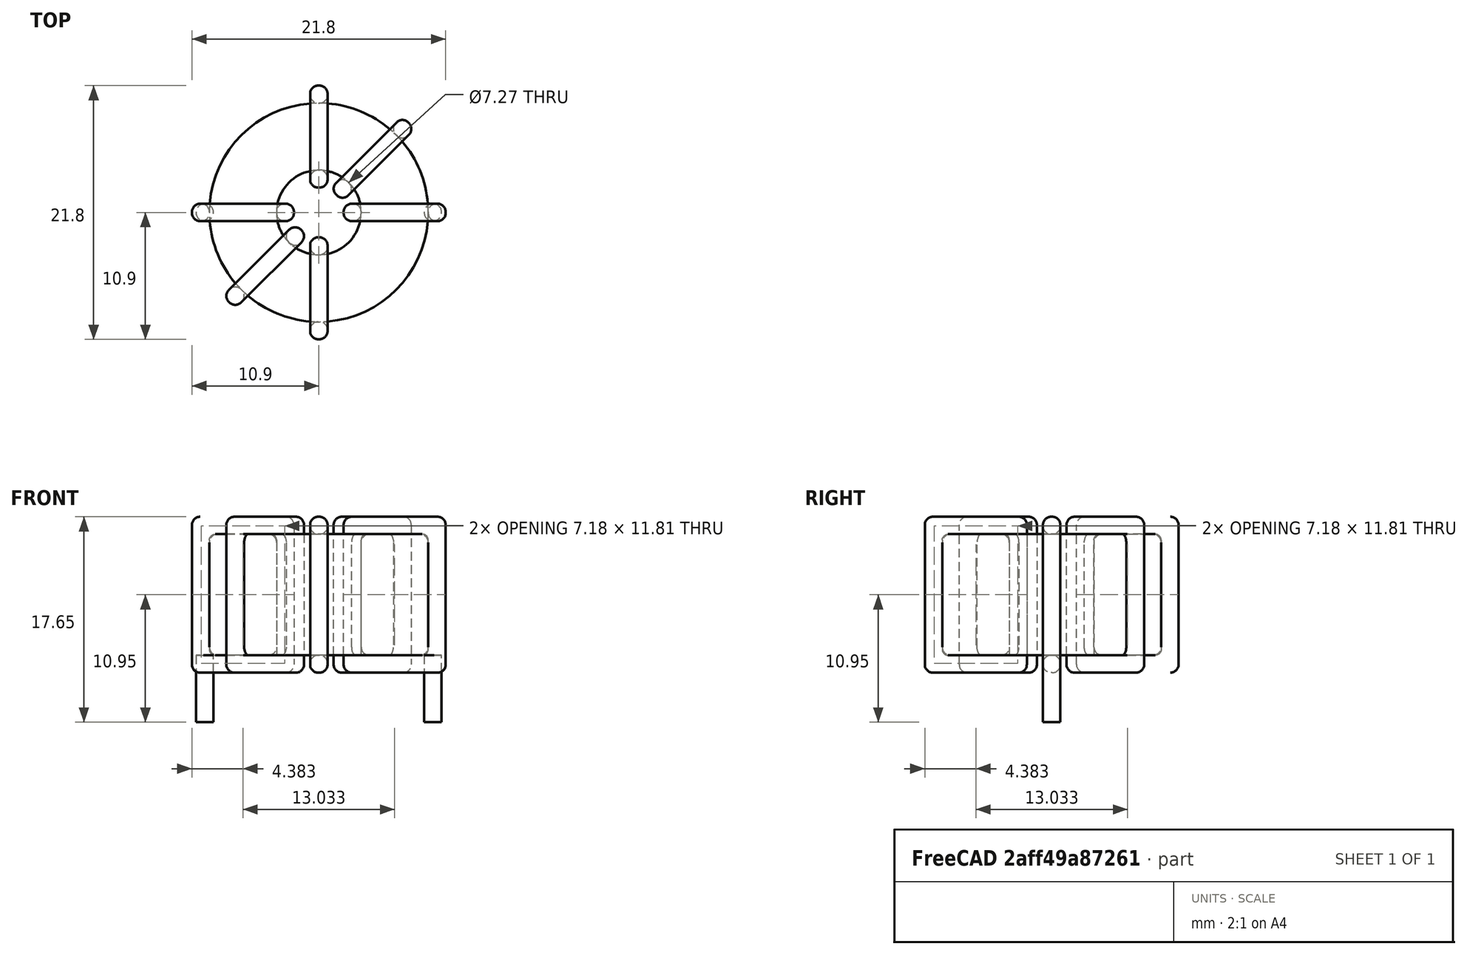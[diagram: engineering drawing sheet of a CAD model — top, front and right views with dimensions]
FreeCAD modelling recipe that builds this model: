
FCSTD DOCUMENT  (FreeCAD 0.16R6703 (Git))
Label: L_Toroid_Horizontal_D21.8mm_P19.60mm_Bourns_2100series
License: All rights reserved
LicenseURL: http://en.wikipedia.org/wiki/All_rights_reserved
objects: Sketcher::SketchObject×6, PartDesign::Pad×6, PartDesign::Fillet×5, Spreadsheet::Sheet×1
note: 23 computed .brp shape members not serialized (recipe doc carries the construction recipe); baked Part::Feature solids carry a one-line shape summary decoded from their .brp

FEATURE [Spreadsheet::Sheet] Spreadsheet  label="dimensions"
  cells = A1=Wx; B1(Wx)=21.8; C1(WW)=7.266666666666667; D1=21.8; A2=Wy; B2(Wy)=21.8; D2=21.8; A3=RM; B3(RMx)=19.6; C3(RMy)=0; A4=d_wire; B4(d_wire)=1.5; A5=H; B5(H)=10.4; A6=offsetx; B6(offsetx)=1.1
FEATURE [Sketcher::SketchObject] Sketch
  Placement = pos=(0,0,2) rot=(0,0,1;0rad)
  expr: Placement.Base.z = 0.5 + Spreadsheet.d_wire
  expr: Constraints[0] = Spreadsheet.Wx / 2 - Spreadsheet.d_wire
  expr: Constraints[4] = Spreadsheet.WW / 2
  expr: Constraints[2] = Spreadsheet.RMy / 2
  expr: Constraints[1] = Spreadsheet.RMx / 2
  sketch-geometry (2):
    g0: Circle CenterX=9.8 CenterY=0 CenterZ=0 NormalX=0 NormalY=0 NormalZ=1 Radius=9.4
    g1: Circle CenterX=9.8 CenterY=0 CenterZ=0 NormalX=0 NormalY=0 NormalZ=1 Radius=3.63333
  constraints (5):
    c: Radius(g0) = 9.4
    c: DistanceX(g-1,g0) = 9.8
    c: DistanceY(g-1,g0) = 0
    c: Coincident(g1,g0)
    c: Radius(g1) = 3.63333
FEATURE [PartDesign::Pad] Pad
  Length = 10.4
  Length2 = 100
  Placement = pos=(0,0,2) rot=(0,0,1;0rad)
  Sketch = -> Sketch
  Type = 0
  expr: Length = Spreadsheet.H
FEATURE [Sketcher::SketchObject] Sketch001
  Placement = pos=(0,0,1.25) rot=(0,0,1;0rad)
  expr: Placement.Base.z = 0.5 + Spreadsheet.d_wire * 0.5
  expr: Constraints[4] = Spreadsheet.RMx
  expr: Constraints[2] = Spreadsheet.RMy
  expr: Constraints[1] = Spreadsheet.d_wire / 2
  sketch-geometry (2):
    g0: Circle CenterX=0 CenterY=0 CenterZ=0 NormalX=0 NormalY=0 NormalZ=1 Radius=0.75
    g1: Circle CenterX=19.6 CenterY=0 CenterZ=0 NormalX=0 NormalY=0 NormalZ=1 Radius=0.75
  constraints (5):
    c: Equal(g0,g1)
    c: Radius(g0) = 0.75
    c: DistanceY(g-1,g1) = 0
    c: Coincident(g0,g-1)
    c: DistanceX(g-1,g1) = 19.6
FEATURE [PartDesign::Pad] Pad001
  Length = 0.75
  Length2 = 5
  Placement = pos=(0,0,1.25) rot=(0,0,1;0rad)
  Reversed = true
  Sketch = -> Sketch001
  Type = 4
  expr: Length2 = 3.5 + Spreadsheet.d_wire
  expr: Length = Spreadsheet.d_wire / 2
FEATURE [PartDesign::Fillet] Fillet
  Base = -> Pad [Edge6,Edge3,Edge2]
  Placement = pos=(0,0,2) rot=(0,0,1;0rad)
  Radius = 0.5
FEATURE [Sketcher::SketchObject] Sketch003
  Placement = pos=(9.8,0,0) rot=(1,0,0;1.5708rad)
  expr: Placement.Base.x = Spreadsheet.RMx / 2
  expr: Constraints[49] = Spreadsheet.Wx - Spreadsheet.d_wire * 2
  expr: Constraints[44] = Spreadsheet.d_wire
  expr: Constraints[23] = Spreadsheet.H
  expr: Constraints[22] = Spreadsheet.Wx / 2 - Spreadsheet.d_wire
  expr: Placement.Base.y = Spreadsheet.RMy / 2
  expr: Constraints[21] = (Spreadsheet.Wx - Spreadsheet.WW) / 2 - Spreadsheet.d_wire
  expr: Constraints[19] = Spreadsheet.d_wire
  expr: Constraints[17] = Spreadsheet.d_wire
  expr: Constraints[18] = Spreadsheet.d_wire
  expr: Constraints[16] = Spreadsheet.d_wire
  sketch-geometry (16):
    g0: LineSegment StartX=-2.13333 StartY=0.5 StartZ=0 EndX=-10.9 EndY=0.5 EndZ=0
    g1: LineSegment StartX=-10.9 StartY=0.5 StartZ=0 EndX=-10.9 EndY=13.9 EndZ=0
    g2: LineSegment StartX=-10.9 StartY=13.9 StartZ=0 EndX=-2.13333 EndY=13.9 EndZ=0
    g3: LineSegment StartX=-2.13333 StartY=13.9 StartZ=0 EndX=-2.13333 EndY=0.5 EndZ=0
    g4: LineSegment StartX=-9.4 StartY=12.4 StartZ=0 EndX=-3.63333 EndY=12.4 EndZ=0
    g5: LineSegment StartX=-3.63333 StartY=12.4 StartZ=0 EndX=-3.63333 EndY=2 EndZ=0
    g6: LineSegment StartX=-3.63333 StartY=2 StartZ=0 EndX=-9.4 EndY=2 EndZ=0
    g7: LineSegment StartX=-9.4 StartY=2 StartZ=0 EndX=-9.4 EndY=12.4 EndZ=0
    g8: LineSegment StartX=2.13333 StartY=13.9 StartZ=0 EndX=10.9 EndY=13.9 EndZ=0
    g9: LineSegment StartX=10.9 StartY=13.9 StartZ=0 EndX=10.9 EndY=0.5 EndZ=0
    g10: LineSegment StartX=10.9 StartY=0.5 StartZ=0 EndX=2.13333 EndY=0.5 EndZ=0
    g11: LineSegment StartX=2.13333 StartY=0.5 StartZ=0 EndX=2.13333 EndY=13.9 EndZ=0
    g12: LineSegment StartX=3.63333 StartY=12.4 StartZ=0 EndX=9.4 EndY=12.4 EndZ=0
    g13: LineSegment StartX=9.4 StartY=12.4 StartZ=0 EndX=9.4 EndY=2 EndZ=0
    g14: LineSegment StartX=9.4 StartY=2 StartZ=0 EndX=3.63333 EndY=2 EndZ=0
    g15: LineSegment StartX=3.63333 StartY=2 StartZ=0 EndX=3.63333 EndY=12.4 EndZ=0
  constraints (50):
    c: Horizontal(g0)
    c: Coincident(g1,g0)
    c: Vertical(g1)
    c: Coincident(g2,g1)
    c: Horizontal(g2)
    c: Coincident(g3,g2)
    c: Coincident(g3,g0)
    c: Vertical(g3)
    c: Coincident(g4,g5)
    c: Coincident(g5,g6)
    c: Coincident(g6,g7)
    c: Coincident(g7,g4)
    c: Horizontal(g4)
    c: Horizontal(g6)
    c: Vertical(g5)
    c: Vertical(g7)
    c: DistanceX(g1,g4) = 1.5
    c: DistanceY(g4,g1) = 1.5
    c: DistanceX(g5,g0) = 1.5
    c: DistanceY(g0,g5) = 1.5
    c: DistanceY(g-1,g0) = 0.5
    c: DistanceX(g6,g6) = 5.76667
    c: DistanceX(g6,g-1) = 9.4
    c: DistanceY(g7,g7) = 10.4
    c: Coincident(g8,g9)
    c: Coincident(g9,g10)
    c: Coincident(g10,g11)
    c: Coincident(g11,g8)
    c: Horizontal(g8)
    c: Horizontal(g10)
    c: Vertical(g9)
    c: Vertical(g11)
    c: Coincident(g12,g13)
    c: Coincident(g13,g14)
    c: Coincident(g14,g15)
    c: Coincident(g15,g12)
    c: Horizontal(g12)
    c: Horizontal(g14)
    c: Vertical(g13)
    c: Vertical(g15)
    c: DistanceY(g8,g2) = 0
    c: DistanceY(g10,g0) = 0
    c: DistanceY(g14,g5) = 0
    c: DistanceY(g12,g4) = 0
    c: DistanceX(g8,g12) = 1.5
    c: Equal(g8,g2)
    c: Equal(g12,g4)
    c: Equal(g9,g1)
    c: Equal(g13,g7)
    c: DistanceX(g4,g12) = 18.8
FEATURE [PartDesign::Pad] Pad002
  Length = 1.5
  Length2 = 100
  Midplane = true
  Placement = pos=(9.8,0,0) rot=(1,0,0;1.5708rad)
  Sketch = -> Sketch003
  Type = 0
  expr: Length = Spreadsheet.d_wire
FEATURE [PartDesign::Fillet] Fillet001
  Base = -> Pad002 [Edge38,Edge41,Edge42,Edge43,Edge29,Edge32,Edge33,Edge34,Edge25,Edge35,Edge36,Edge13,Edge14,Edge15,Edge16,Edge17,Edge18,Edge19,Edge1,Edge2,Edge3,Edge4,Edge5,Edge6,Edge7,Edge37,Edge39,Edge40,Edge20,Edge23,Edge24,Edge21,Edge22,Edge8,Edge9,Edge10,Edge11,Edge12,Edge26,Edge27,+8 more]
  Placement = pos=(9.8,0,0) rot=(1,0,0;1.5708rad)
  Radius = 0.705
  expr: Radius = Spreadsheet.d_wire * 0.47
FEATURE [Sketcher::SketchObject] Sketch004
  Placement = pos=(9.8,0,0) rot=(0.862856,0.357407,0.357407;1.71777rad)
  expr: Placement.Base.x = Spreadsheet.RMx / 2
  expr: Constraints[49] = Spreadsheet.Wx - 2 * Spreadsheet.d_wire
  expr: Constraints[44] = Spreadsheet.d_wire
  expr: Constraints[23] = Spreadsheet.H
  expr: Constraints[22] = Spreadsheet.Wx / 2 - Spreadsheet.d_wire
  expr: Placement.Base.y = Spreadsheet.RMy / 2
  expr: Constraints[21] = (Spreadsheet.Wx - Spreadsheet.WW) / 2 - Spreadsheet.d_wire
  expr: Constraints[19] = Spreadsheet.d_wire
  expr: Constraints[17] = Spreadsheet.d_wire
  expr: Constraints[18] = Spreadsheet.d_wire
  expr: Constraints[16] = Spreadsheet.d_wire
  sketch-geometry (16):
    g0: LineSegment StartX=-2.13333 StartY=0.5 StartZ=0 EndX=-10.9 EndY=0.5 EndZ=0
    g1: LineSegment StartX=-10.9 StartY=0.5 StartZ=0 EndX=-10.9 EndY=13.9 EndZ=0
    g2: LineSegment StartX=-10.9 StartY=13.9 StartZ=0 EndX=-2.13333 EndY=13.9 EndZ=0
    g3: LineSegment StartX=-2.13333 StartY=13.9 StartZ=0 EndX=-2.13333 EndY=0.5 EndZ=0
    g4: LineSegment StartX=-9.4 StartY=12.4 StartZ=0 EndX=-3.63333 EndY=12.4 EndZ=0
    g5: LineSegment StartX=-3.63333 StartY=12.4 StartZ=0 EndX=-3.63333 EndY=2 EndZ=0
    g6: LineSegment StartX=-3.63333 StartY=2 StartZ=0 EndX=-9.4 EndY=2 EndZ=0
    g7: LineSegment StartX=-9.4 StartY=2 StartZ=0 EndX=-9.4 EndY=12.4 EndZ=0
    g8: LineSegment StartX=2.13333 StartY=13.9 StartZ=0 EndX=10.9 EndY=13.9 EndZ=0
    g9: LineSegment StartX=10.9 StartY=13.9 StartZ=0 EndX=10.9 EndY=0.5 EndZ=0
    g10: LineSegment StartX=10.9 StartY=0.5 StartZ=0 EndX=2.13333 EndY=0.5 EndZ=0
    g11: LineSegment StartX=2.13333 StartY=0.5 StartZ=0 EndX=2.13333 EndY=13.9 EndZ=0
    g12: LineSegment StartX=3.63333 StartY=12.4 StartZ=0 EndX=9.4 EndY=12.4 EndZ=0
    g13: LineSegment StartX=9.4 StartY=12.4 StartZ=0 EndX=9.4 EndY=2 EndZ=0
    g14: LineSegment StartX=9.4 StartY=2 StartZ=0 EndX=3.63333 EndY=2 EndZ=0
    g15: LineSegment StartX=3.63333 StartY=2 StartZ=0 EndX=3.63333 EndY=12.4 EndZ=0
  constraints (50):
    c: Horizontal(g0)
    c: Coincident(g1,g0)
    c: Vertical(g1)
    c: Coincident(g2,g1)
    c: Horizontal(g2)
    c: Coincident(g3,g2)
    c: Coincident(g3,g0)
    c: Vertical(g3)
    c: Coincident(g4,g5)
    c: Coincident(g5,g6)
    c: Coincident(g6,g7)
    c: Coincident(g7,g4)
    c: Horizontal(g4)
    c: Horizontal(g6)
    c: Vertical(g5)
    c: Vertical(g7)
    c: DistanceX(g1,g4) = 1.5
    c: DistanceY(g4,g1) = 1.5
    c: DistanceX(g5,g0) = 1.5
    c: DistanceY(g0,g5) = 1.5
    c: DistanceY(g-1,g0) = 0.5
    c: DistanceX(g6,g6) = 5.76667
    c: DistanceX(g6,g-1) = 9.4
    c: DistanceY(g7,g7) = 10.4
    c: Coincident(g8,g9)
    c: Coincident(g9,g10)
    c: Coincident(g10,g11)
    c: Coincident(g11,g8)
    c: Horizontal(g8)
    c: Horizontal(g10)
    c: Vertical(g9)
    c: Vertical(g11)
    c: Coincident(g12,g13)
    c: Coincident(g13,g14)
    c: Coincident(g14,g15)
    c: Coincident(g15,g12)
    c: Horizontal(g12)
    c: Horizontal(g14)
    c: Vertical(g13)
    c: Vertical(g15)
    c: DistanceY(g8,g2) = 0
    c: DistanceY(g10,g0) = 0
    c: DistanceY(g14,g5) = 0
    c: DistanceY(g12,g4) = 0
    c: DistanceX(g8,g12) = 1.5
    c: Equal(g8,g2)
    c: Equal(g12,g4)
    c: Equal(g9,g1)
    c: Equal(g13,g7)
    c: DistanceX(g4,g12) = 18.8
FEATURE [PartDesign::Pad] Pad003
  Length = 1.5
  Length2 = 100
  Midplane = true
  Placement = pos=(9.8,0,0) rot=(0.862856,0.357407,0.357407;1.71777rad)
  Sketch = -> Sketch004
  Type = 0
  expr: Length = Spreadsheet.d_wire
FEATURE [PartDesign::Fillet] Fillet002
  Base = -> Pad003 [Edge38,Edge41,Edge42,Edge43,Edge29,Edge32,Edge33,Edge34,Edge25,Edge35,Edge36,Edge13,Edge14,Edge15,Edge16,Edge17,Edge18,Edge19,Edge1,Edge2,Edge3,Edge4,Edge5,Edge6,Edge7,Edge37,Edge39,Edge40,Edge20,Edge23,Edge24,Edge21,Edge22,Edge8,Edge9,Edge10,Edge11,Edge12,Edge26,Edge27,+8 more]
  Placement = pos=(9.8,0,0) rot=(0.862856,0.357407,0.357407;1.71777rad)
  Radius = 0.705
  expr: Radius = Spreadsheet.d_wire * 0.47
FEATURE [Sketcher::SketchObject] Sketch005
  Placement = pos=(9.8,0,0) rot=(0.862856,-0.357407,-0.357407;1.71777rad)
  expr: Placement.Base.x = Spreadsheet.RMx / 2
  expr: Constraints[49] = Spreadsheet.Wx - 2 * Spreadsheet.d_wire
  expr: Constraints[44] = Spreadsheet.d_wire
  expr: Constraints[23] = Spreadsheet.H
  expr: Constraints[22] = Spreadsheet.Wx / 2 - Spreadsheet.d_wire
  expr: Placement.Base.y = Spreadsheet.RMy / 2
  expr: Constraints[21] = (Spreadsheet.Wx - Spreadsheet.WW) / 2 - Spreadsheet.d_wire
  expr: Constraints[19] = Spreadsheet.d_wire
  expr: Constraints[17] = Spreadsheet.d_wire
  expr: Constraints[18] = Spreadsheet.d_wire
  expr: Constraints[16] = Spreadsheet.d_wire
  sketch-geometry (16):
    g0: LineSegment StartX=-2.13333 StartY=0.5 StartZ=0 EndX=-10.9 EndY=0.5 EndZ=0
    g1: LineSegment StartX=-10.9 StartY=0.5 StartZ=0 EndX=-10.9 EndY=13.9 EndZ=0
    g2: LineSegment StartX=-10.9 StartY=13.9 StartZ=0 EndX=-2.13333 EndY=13.9 EndZ=0
    g3: LineSegment StartX=-2.13333 StartY=13.9 StartZ=0 EndX=-2.13333 EndY=0.5 EndZ=0
    g4: LineSegment StartX=-9.4 StartY=12.4 StartZ=0 EndX=-3.63333 EndY=12.4 EndZ=0
    g5: LineSegment StartX=-3.63333 StartY=12.4 StartZ=0 EndX=-3.63333 EndY=2 EndZ=0
    g6: LineSegment StartX=-3.63333 StartY=2 StartZ=0 EndX=-9.4 EndY=2 EndZ=0
    g7: LineSegment StartX=-9.4 StartY=2 StartZ=0 EndX=-9.4 EndY=12.4 EndZ=0
    g8: LineSegment StartX=2.13333 StartY=13.9 StartZ=0 EndX=10.9 EndY=13.9 EndZ=0
    g9: LineSegment StartX=10.9 StartY=13.9 StartZ=0 EndX=10.9 EndY=0.5 EndZ=0
    g10: LineSegment StartX=10.9 StartY=0.5 StartZ=0 EndX=2.13333 EndY=0.5 EndZ=0
    g11: LineSegment StartX=2.13333 StartY=0.5 StartZ=0 EndX=2.13333 EndY=13.9 EndZ=0
    g12: LineSegment StartX=3.63333 StartY=12.4 StartZ=0 EndX=9.4 EndY=12.4 EndZ=0
    g13: LineSegment StartX=9.4 StartY=12.4 StartZ=0 EndX=9.4 EndY=2 EndZ=0
    g14: LineSegment StartX=9.4 StartY=2 StartZ=0 EndX=3.63333 EndY=2 EndZ=0
    g15: LineSegment StartX=3.63333 StartY=2 StartZ=0 EndX=3.63333 EndY=12.4 EndZ=0
  constraints (50):
    c: Horizontal(g0)
    c: Coincident(g1,g0)
    c: Vertical(g1)
    c: Coincident(g2,g1)
    c: Horizontal(g2)
    c: Coincident(g3,g2)
    c: Coincident(g3,g0)
    c: Vertical(g3)
    c: Coincident(g4,g5)
    c: Coincident(g5,g6)
    c: Coincident(g6,g7)
    c: Coincident(g7,g4)
    c: Horizontal(g4)
    c: Horizontal(g6)
    c: Vertical(g5)
    c: Vertical(g7)
    c: DistanceX(g1,g4) = 1.5
    c: DistanceY(g4,g1) = 1.5
    c: DistanceX(g5,g0) = 1.5
    c: DistanceY(g0,g5) = 1.5
    c: DistanceY(g-1,g0) = 0.5
    c: DistanceX(g6,g6) = 5.76667
    c: DistanceX(g6,g-1) = 9.4
    c: DistanceY(g7,g7) = 10.4
    c: Coincident(g8,g9)
    c: Coincident(g9,g10)
    c: Coincident(g10,g11)
    c: Coincident(g11,g8)
    c: Horizontal(g8)
    c: Horizontal(g10)
    c: Vertical(g9)
    c: Vertical(g11)
    c: Coincident(g12,g13)
    c: Coincident(g13,g14)
    c: Coincident(g14,g15)
    c: Coincident(g15,g12)
    c: Horizontal(g12)
    c: Horizontal(g14)
    c: Vertical(g13)
    c: Vertical(g15)
    c: DistanceY(g8,g2) = 0
    c: DistanceY(g10,g0) = 0
    c: DistanceY(g14,g5) = 0
    c: DistanceY(g12,g4) = 0
    c: DistanceX(g8,g12) = 1.5
    c: Equal(g8,g2)
    c: Equal(g12,g4)
    c: Equal(g9,g1)
    c: Equal(g13,g7)
    c: DistanceX(g4,g12) = 18.8
FEATURE [PartDesign::Pad] Pad004
  Length = 1.5
  Length2 = 100
  Midplane = true
  Placement = pos=(9.8,0,0) rot=(0.862856,-0.357407,-0.357407;1.71777rad)
  Sketch = -> Sketch005
  Type = 0
  expr: Length = Spreadsheet.d_wire
FEATURE [PartDesign::Fillet] Fillet003
  Base = -> Pad004 [Edge38,Edge41,Edge42,Edge43,Edge29,Edge32,Edge33,Edge34,Edge25,Edge35,Edge36,Edge13,Edge14,Edge15,Edge16,Edge17,Edge18,Edge19,Edge1,Edge2,Edge3,Edge4,Edge5,Edge6,Edge7,Edge37,Edge39,Edge40,Edge20,Edge23,Edge24,Edge21,Edge22,Edge8,Edge9,Edge10,Edge11,Edge12,Edge26,Edge27,+8 more]
  Placement = pos=(9.8,0,0) rot=(0.862856,-0.357407,-0.357407;1.71777rad)
  Radius = 0.705
  expr: Radius = Spreadsheet.d_wire * 0.47
FEATURE [Sketcher::SketchObject] Sketch006
  Placement = pos=(9.8,0,0) rot=(0.57735,0.57735,0.57735;2.0944rad)
  expr: Placement.Base.x = Spreadsheet.RMx / 2
  expr: Constraints[49] = Spreadsheet.Wx - Spreadsheet.d_wire * 2
  expr: Constraints[44] = Spreadsheet.d_wire
  expr: Constraints[23] = Spreadsheet.H
  expr: Constraints[22] = Spreadsheet.Wx / 2 - Spreadsheet.d_wire
  expr: Placement.Base.y = Spreadsheet.RMy / 2
  expr: Constraints[21] = (Spreadsheet.Wx - Spreadsheet.WW) / 2 - Spreadsheet.d_wire
  expr: Constraints[19] = Spreadsheet.d_wire
  expr: Constraints[17] = Spreadsheet.d_wire
  expr: Constraints[18] = Spreadsheet.d_wire
  expr: Constraints[16] = Spreadsheet.d_wire
  sketch-geometry (16):
    g0: LineSegment StartX=-2.13333 StartY=0.5 StartZ=0 EndX=-10.9 EndY=0.5 EndZ=0
    g1: LineSegment StartX=-10.9 StartY=0.5 StartZ=0 EndX=-10.9 EndY=13.9 EndZ=0
    g2: LineSegment StartX=-10.9 StartY=13.9 StartZ=0 EndX=-2.13333 EndY=13.9 EndZ=0
    g3: LineSegment StartX=-2.13333 StartY=13.9 StartZ=0 EndX=-2.13333 EndY=0.5 EndZ=0
    g4: LineSegment StartX=-9.4 StartY=12.4 StartZ=0 EndX=-3.63333 EndY=12.4 EndZ=0
    g5: LineSegment StartX=-3.63333 StartY=12.4 StartZ=0 EndX=-3.63333 EndY=2 EndZ=0
    g6: LineSegment StartX=-3.63333 StartY=2 StartZ=0 EndX=-9.4 EndY=2 EndZ=0
    g7: LineSegment StartX=-9.4 StartY=2 StartZ=0 EndX=-9.4 EndY=12.4 EndZ=0
    g8: LineSegment StartX=2.13333 StartY=13.9 StartZ=0 EndX=10.9 EndY=13.9 EndZ=0
    g9: LineSegment StartX=10.9 StartY=13.9 StartZ=0 EndX=10.9 EndY=0.5 EndZ=0
    g10: LineSegment StartX=10.9 StartY=0.5 StartZ=0 EndX=2.13333 EndY=0.5 EndZ=0
    g11: LineSegment StartX=2.13333 StartY=0.5 StartZ=0 EndX=2.13333 EndY=13.9 EndZ=0
    g12: LineSegment StartX=3.63333 StartY=12.4 StartZ=0 EndX=9.4 EndY=12.4 EndZ=0
    g13: LineSegment StartX=9.4 StartY=12.4 StartZ=0 EndX=9.4 EndY=2 EndZ=0
    g14: LineSegment StartX=9.4 StartY=2 StartZ=0 EndX=3.63333 EndY=2 EndZ=0
    g15: LineSegment StartX=3.63333 StartY=2 StartZ=0 EndX=3.63333 EndY=12.4 EndZ=0
  constraints (50):
    c: Horizontal(g0)
    c: Coincident(g1,g0)
    c: Vertical(g1)
    c: Coincident(g2,g1)
    c: Horizontal(g2)
    c: Coincident(g3,g2)
    c: Coincident(g3,g0)
    c: Vertical(g3)
    c: Coincident(g4,g5)
    c: Coincident(g5,g6)
    c: Coincident(g6,g7)
    c: Coincident(g7,g4)
    c: Horizontal(g4)
    c: Horizontal(g6)
    c: Vertical(g5)
    c: Vertical(g7)
    c: DistanceX(g1,g4) = 1.5
    c: DistanceY(g4,g1) = 1.5
    c: DistanceX(g5,g0) = 1.5
    c: DistanceY(g0,g5) = 1.5
    c: DistanceY(g-1,g0) = 0.5
    c: DistanceX(g6,g6) = 5.76667
    c: DistanceX(g6,g-1) = 9.4
    c: DistanceY(g7,g7) = 10.4
    c: Coincident(g8,g9)
    c: Coincident(g9,g10)
    c: Coincident(g10,g11)
    c: Coincident(g11,g8)
    c: Horizontal(g8)
    c: Horizontal(g10)
    c: Vertical(g9)
    c: Vertical(g11)
    c: Coincident(g12,g13)
    c: Coincident(g13,g14)
    c: Coincident(g14,g15)
    c: Coincident(g15,g12)
    c: Horizontal(g12)
    c: Horizontal(g14)
    c: Vertical(g13)
    c: Vertical(g15)
    c: DistanceY(g8,g2) = 0
    c: DistanceY(g10,g0) = 0
    c: DistanceY(g14,g5) = 0
    c: DistanceY(g12,g4) = 0
    c: DistanceX(g8,g12) = 1.5
    c: Equal(g8,g2)
    c: Equal(g12,g4)
    c: Equal(g9,g1)
    c: Equal(g13,g7)
    c: DistanceX(g4,g12) = 18.8
FEATURE [PartDesign::Pad] Pad005
  Length = 1.5
  Length2 = 100
  Midplane = true
  Placement = pos=(9.8,0,0) rot=(0.57735,0.57735,0.57735;2.0944rad)
  Sketch = -> Sketch006
  Type = 0
  expr: Length = Spreadsheet.d_wire
FEATURE [PartDesign::Fillet] Fillet004
  Base = -> Pad005 [Edge38,Edge41,Edge42,Edge43,Edge29,Edge32,Edge33,Edge34,Edge25,Edge35,Edge36,Edge13,Edge14,Edge15,Edge16,Edge17,Edge18,Edge19,Edge1,Edge2,Edge3,Edge4,Edge5,Edge6,Edge7,Edge37,Edge39,Edge40,Edge20,Edge23,Edge24,Edge21,Edge22,Edge8,Edge9,Edge10,Edge11,Edge12,Edge26,Edge27,+8 more]
  Placement = pos=(9.8,0,0) rot=(0.57735,0.57735,0.57735;2.0944rad)
  Radius = 0.705
  expr: Radius = Spreadsheet.d_wire * 0.47
